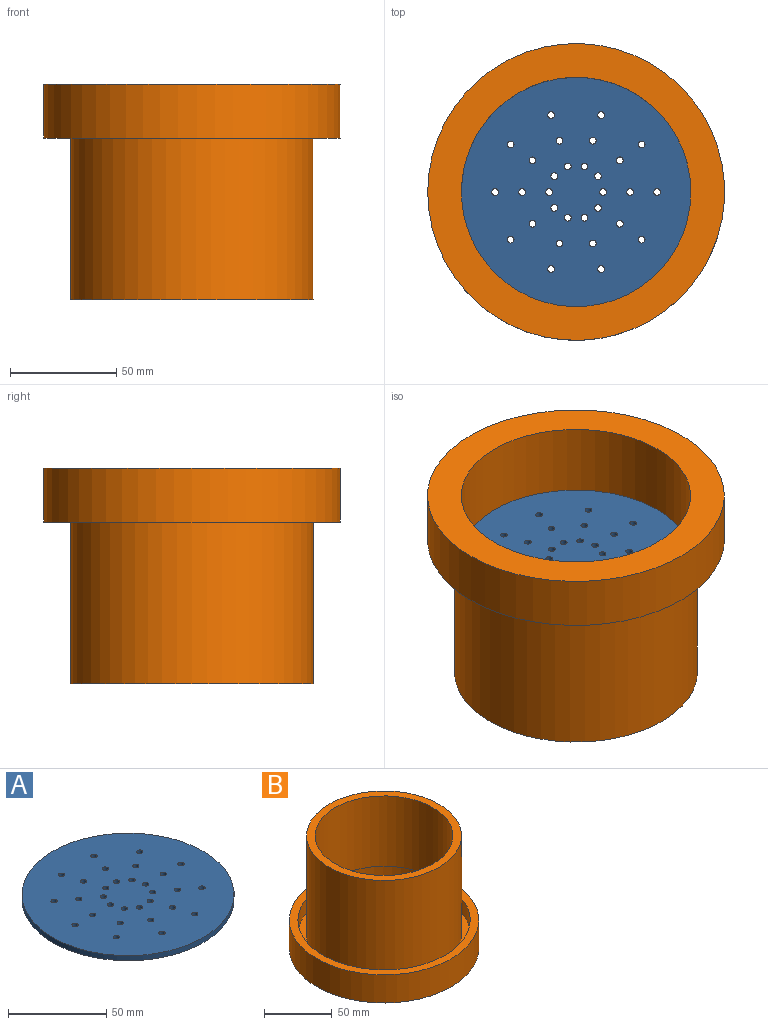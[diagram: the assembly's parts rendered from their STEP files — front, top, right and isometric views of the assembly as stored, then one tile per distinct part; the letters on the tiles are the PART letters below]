
ASSEMBLY  parts=2 mates=1
PART A: 33 faces, bbox 108x108x3.2 mm
  f0: cylinder r=1.59mm len=3.18mm, axis (0,0,-1), area 31.7mm2, adj f31,f32
  f1: cylinder r=1.59mm len=3.18mm, axis (0,0,-1), area 31.7mm2, adj f31,f32
  f2: cylinder r=1.59mm len=3.18mm, axis (0,0,-1), area 31.7mm2, adj f31,f32
  f3: cylinder r=1.59mm len=3.18mm, axis (0,0,-1), area 31.7mm2, adj f31,f32
  f4: cylinder r=1.59mm len=3.18mm, axis (0,0,-1), area 31.7mm2, adj f31,f32
  f5: cylinder r=1.59mm len=3.18mm, axis (0,0,-1), area 31.7mm2, adj f31,f32
  f6: cylinder r=1.59mm len=3.18mm, axis (0,0,-1), area 31.7mm2, adj f31,f32
  f7: cylinder r=1.59mm len=3.18mm, axis (0,0,-1), area 31.7mm2, adj f31,f32
  f8: cylinder r=1.59mm len=3.18mm, axis (0,0,-1), area 31.7mm2, adj f31,f32
  f9: cylinder r=1.59mm len=3.18mm, axis (0,0,-1), area 31.7mm2, adj f31,f32
  f10: cylinder r=1.59mm len=3.18mm, axis (0,0,-1), area 31.7mm2, adj f31,f32
  f11: cylinder r=1.59mm len=3.18mm, axis (0,0,-1), area 31.7mm2, adj f31,f32
  f12: cylinder r=1.59mm len=3.18mm, axis (0,0,-1), area 31.7mm2, adj f31,f32
  f13: cylinder r=1.59mm len=3.18mm, axis (0,0,-1), area 31.7mm2, adj f31,f32
  f14: cylinder r=1.59mm len=3.18mm, axis (0,0,-1), area 31.7mm2, adj f31,f32
  f15: cylinder r=1.59mm len=3.18mm, axis (0,0,-1), area 31.7mm2, adj f31,f32
  f16: cylinder r=1.59mm len=3.18mm, axis (0,0,-1), area 31.7mm2, adj f31,f32
  f17: cylinder r=1.59mm len=3.18mm, axis (0,0,-1), area 31.7mm2, adj f31,f32
  f18: cylinder r=1.59mm len=3.18mm, axis (0,0,-1), area 31.7mm2, adj f31,f32
  f19: cylinder r=1.59mm len=3.18mm, axis (0,0,-1), area 31.7mm2, adj f31,f32
  f20: cylinder r=1.59mm len=3.18mm, axis (0,0,-1), area 31.7mm2, adj f31,f32
  f21: cylinder r=1.59mm len=3.18mm, axis (0,0,-1), area 31.7mm2, adj f31,f32
  f22: cylinder r=1.59mm len=3.18mm, axis (0,0,-1), area 31.7mm2, adj f31,f32
  f23: cylinder r=1.59mm len=3.18mm, axis (0,0,-1), area 31.7mm2, adj f31,f32
  f24: cylinder r=1.59mm len=3.18mm, axis (0,0,-1), area 31.7mm2, adj f31,f32
  f25: cylinder r=1.59mm len=3.18mm, axis (0,0,-1), area 31.7mm2, adj f31,f32
  f26: cylinder r=1.59mm len=3.18mm, axis (0,0,-1), area 31.7mm2, adj f31,f32
  f27: cylinder r=1.59mm len=3.18mm, axis (0,0,-1), area 31.7mm2, adj f31,f32
  f28: cylinder r=1.59mm len=3.18mm, axis (0,0,-1), area 31.7mm2, adj f31,f32
  f29: cylinder r=1.59mm len=3.18mm, axis (0,0,-1), area 31.7mm2, adj f31,f32
  f30: cylinder r=53.98mm len=107.95mm, axis (0,0,-1), area 1076.8mm2, adj f31,f32
  f31: plane 107.95x107.95mm, normal (0,0,1), area 8914.9mm2, adj f0,f1,f2,f3,f4,f5,f6,f7
  f32: plane 107.95x107.95mm, normal (0,0,-1), area 8914.9mm2, adj f0,f1,f2,f3,f4,f5,f6,f7
PART B: 10 faces, bbox 139.7x139.7x101.6 mm
  f0: cylinder r=50.8mm len=101.6mm, axis (0,0,-1), area 20268.3mm2, adj f2,f9
  f1: cylinder r=57.15mm len=114.3mm, axis (0,0,-1), area 31922.6mm2, adj f2,f7
  f2: plane 114.3x114.3mm, normal (0,0,1), area 2153.5mm2, adj f0,f1
  f3: plane 139.7x139.7mm, normal (0,0,-1), area 6175.5mm2, adj f4,f8
  f4: cylinder r=69.85mm len=139.7mm, axis (0,0,-1), area 11147.6mm2, adj f3,f5
  f5: plane 139.7x139.7mm, normal (0,0,1), area 2660.2mm2, adj f4,f6
  f6: cylinder r=63.5mm len=127mm, axis (0,0,1), area 5067.1mm2, adj f5,f7
  f7: plane 127x127mm, normal (0,0,1), area 2406.9mm2, adj f1,f6
  f8: cylinder r=53.98mm len=107.95mm, axis (0,0,-1), area 12921mm2, adj f3,f9
  f9: plane 107.95x107.95mm, normal (0,0,-1), area 1045.1mm2, adj f0,f8
PLACE A t=(80.35,42.35,-49.2)mm
PLACE B rot(axis=(0,1,0),180deg) t=(80.35,42.35,-11.1)mm
MATE fastened B.f0 <-> A.f30  axis (0,0,1) through (80.35,42.35,-49.2)mm
